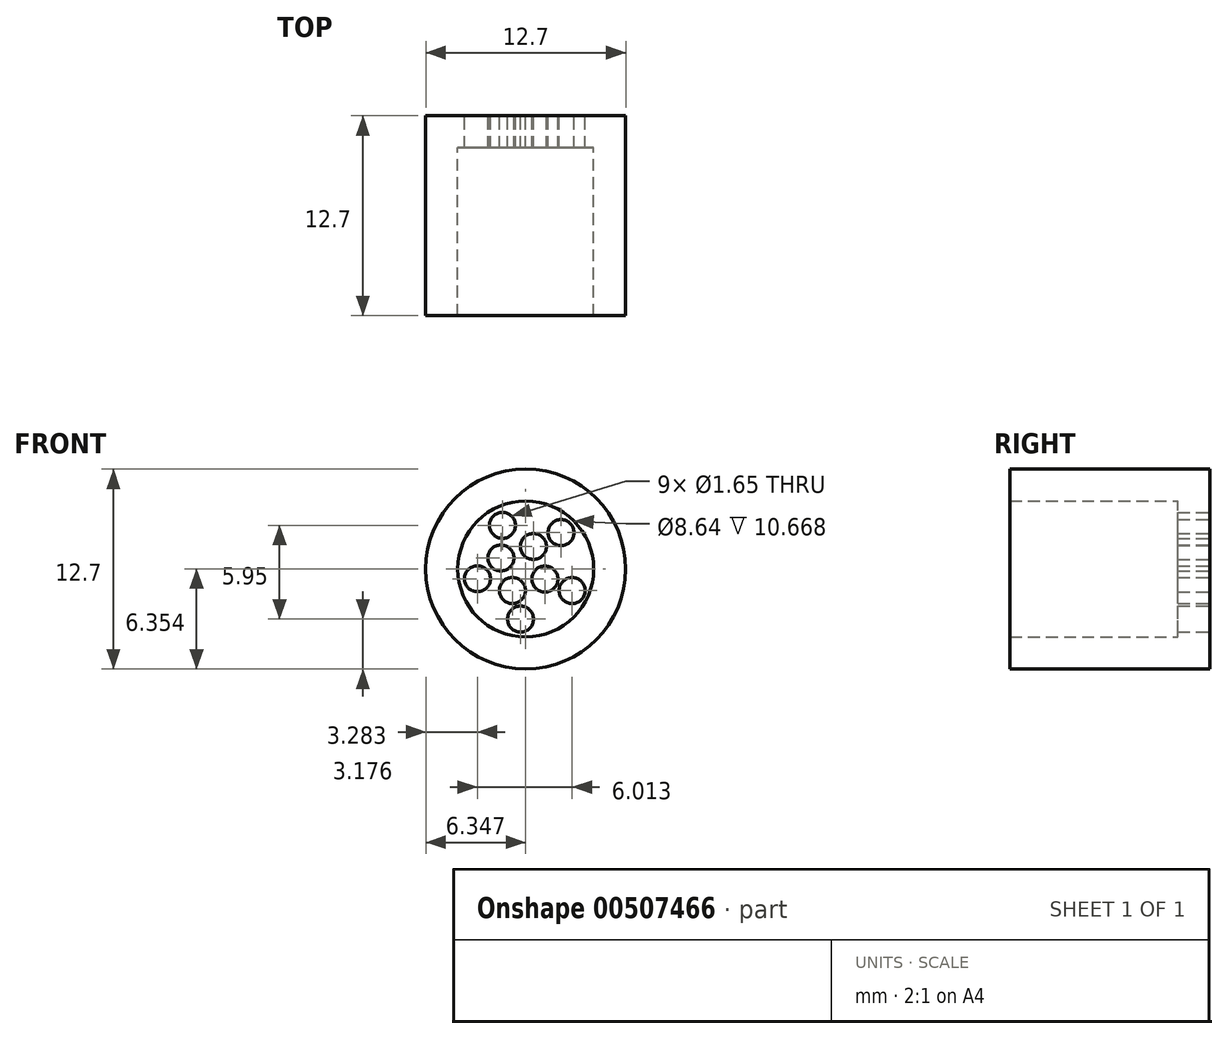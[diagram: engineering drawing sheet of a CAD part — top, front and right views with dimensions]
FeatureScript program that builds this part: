
annotation { "Feature Type Name" : "Feature", "Feature Type Description" : "" }
export const myFeature = defineFeature(function(context is Context, id is Id, definition is map)
    precondition{}
    {
        {
            var Q0;
            Q0=qCreatedBy(makeId("Front.planeOp"),FACE);
            var sketch = newSketch(context, id + "F0", { "sketchPlane" : qUnion([Q0])});
            skCircle(sketch, "E0", {"center": v(-39.84, 36.6) * mm, "radius": 6.35 * mm});
            skSolve(sketch);
        }
        {
            var Q0;
            Q0 = qSketchRegion(id + "F0", true);
            extrude(context, id + "F1", {"entities" : qUnion([Q0]), "depth" : 12.7 * mm});
        }
        {
            var Q0;
            Q0=makeQuery(id+"F1.opExtrude","CAP_FACE",FACE,{"disambiguationData":[OSD([sQuery(id+"F0.wireOp",EDGE,"E0")])],"isStart":false});
            shell(context, id + "F2", {"entities" : qUnion([Q0]), "thickness" : 2.03 * mm});
        }
        {
            var Q0;
            Q0=qCreatedBy(makeId("Front.planeOp"),FACE);
            var sketch = newSketch(context, id + "F3", { "sketchPlane" : qUnion([Q0])});
            skCircle(sketch, "E1", {"center": v(-36.9, 35.24) * mm, "radius": 0.83 * mm});
            skCircle(sketch, "E2.1.0", {"center": v(-37.6, 38.91) * mm, "radius": 0.83 * mm});
            skCircle(sketch, "E2.2.0", {"center": v(-41.32, 39.38) * mm, "radius": 0.83 * mm});
            skCircle(sketch, "E2.3.0", {"center": v(-42.9, 35.99) * mm, "radius": 0.83 * mm});
            skCircle(sketch, "E2.4.0", {"center": v(-40.17, 33.43) * mm, "radius": 0.83 * mm});
            skPoint(sketch, "E2.center", {"position": v(-39.78, 36.59) * mm});
            skSolve(sketch);
        }
        {
            var Q0;
            Q0=makeQuery(id+"F3.imprint","IMPRINT",FACE,{"disambiguationData":[TD([[makeQuery(id+"F3.imprint","IMPRINT",EDGE,{"derivedFrom":sQuery(id+"F3.wireOp",EDGE,"E2.9.0")}),1.0]])]});
            var Q1;
            Q1=makeQuery(id+"F3.imprint","IMPRINT",FACE,{"disambiguationData":[TD([[makeQuery(id+"F3.imprint","IMPRINT",EDGE,{"derivedFrom":sQuery(id+"F3.wireOp",EDGE,"E2.8.0")}),1.0]])]});
            var Q2;
            Q2=makeQuery(id+"F3.imprint","IMPRINT",FACE,{"disambiguationData":[TD([[makeQuery(id+"F3.imprint","IMPRINT",EDGE,{"derivedFrom":sQuery(id+"F3.wireOp",EDGE,"E2.7.0")}),1.0]])]});
            var Q3;
            Q3=makeQuery(id+"F3.imprint","IMPRINT",FACE,{"disambiguationData":[TD([[makeQuery(id+"F3.imprint","IMPRINT",EDGE,{"derivedFrom":sQuery(id+"F3.wireOp",EDGE,"E2.6.0")}),1.0]])]});
            var Q4;
            Q4=makeQuery(id+"F3.imprint","IMPRINT",FACE,{"disambiguationData":[TD([[makeQuery(id+"F3.imprint","IMPRINT",EDGE,{"derivedFrom":sQuery(id+"F3.wireOp",EDGE,"E2.5.0")}),1.0]])]});
            var Q5;
            Q5=makeQuery(id+"F3.imprint","IMPRINT",FACE,{"disambiguationData":[TD([[makeQuery(id+"F3.imprint","IMPRINT",EDGE,{"derivedFrom":sQuery(id+"F3.wireOp",EDGE,"E2.4.0")}),1.0]])]});
            var Q6;
            Q6=makeQuery(id+"F3.imprint","IMPRINT",FACE,{"disambiguationData":[TD([[makeQuery(id+"F3.imprint","IMPRINT",EDGE,{"derivedFrom":sQuery(id+"F3.wireOp",EDGE,"E2.3.0")}),1.0]])]});
            var Q7;
            Q7=makeQuery(id+"F3.imprint","IMPRINT",FACE,{"disambiguationData":[TD([[makeQuery(id+"F3.imprint","IMPRINT",EDGE,{"derivedFrom":sQuery(id+"F3.wireOp",EDGE,"E2.2.0")}),1.0]])]});
            var Q8;
            Q8=makeQuery(id+"F3.imprint","IMPRINT",FACE,{"disambiguationData":[TD([[makeQuery(id+"F3.imprint","IMPRINT",EDGE,{"derivedFrom":sQuery(id+"F3.wireOp",EDGE,"E2.1.0")}),1.0]])]});
            var Q9;
            Q9=makeQuery(id+"F3.imprint","IMPRINT",FACE,{"disambiguationData":[TD([[makeQuery(id+"F3.imprint","IMPRINT",EDGE,{"derivedFrom":sQuery(id+"F3.wireOp",EDGE,"E1")}),1.0]])]});
            extrude(context, id + "F4", {"entities" : qUnion([Q0, Q1, Q2, Q3, Q4, Q5, Q6, Q7, Q8, Q9]), "operationType" : NewBodyOperationType.REMOVE, "depth" : 25.4 * mm});
        }
        {
            var Q0;
            Q0=qCreatedBy(makeId("Front.planeOp"),FACE);
            var sketch = newSketch(context, id + "F5", { "sketchPlane" : qUnion([Q0])});
            skCircle(sketch, "E3", {"center": v(-38.62, 35.97) * mm, "radius": 0.83 * mm});
            skCircle(sketch, "E4.1.0", {"center": v(-39.35, 38.03) * mm, "radius": 0.83 * mm});
            skCircle(sketch, "E4.2.0", {"center": v(-41.42, 37.3) * mm, "radius": 0.83 * mm});
            skCircle(sketch, "E4.3.0", {"center": v(-40.69, 35.24) * mm, "radius": 0.83 * mm});
            skPoint(sketch, "E4.center", {"position": v(-40.02, 36.64) * mm});
            skSolve(sketch);
        }
        {
            var Q0;
            Q0 = qSketchRegion(id + "F5", true);
            extrude(context, id + "F6", {"entities" : qUnion([Q0]), "operationType" : NewBodyOperationType.REMOVE, "depth" : 25.4 * mm});
        }
    });
